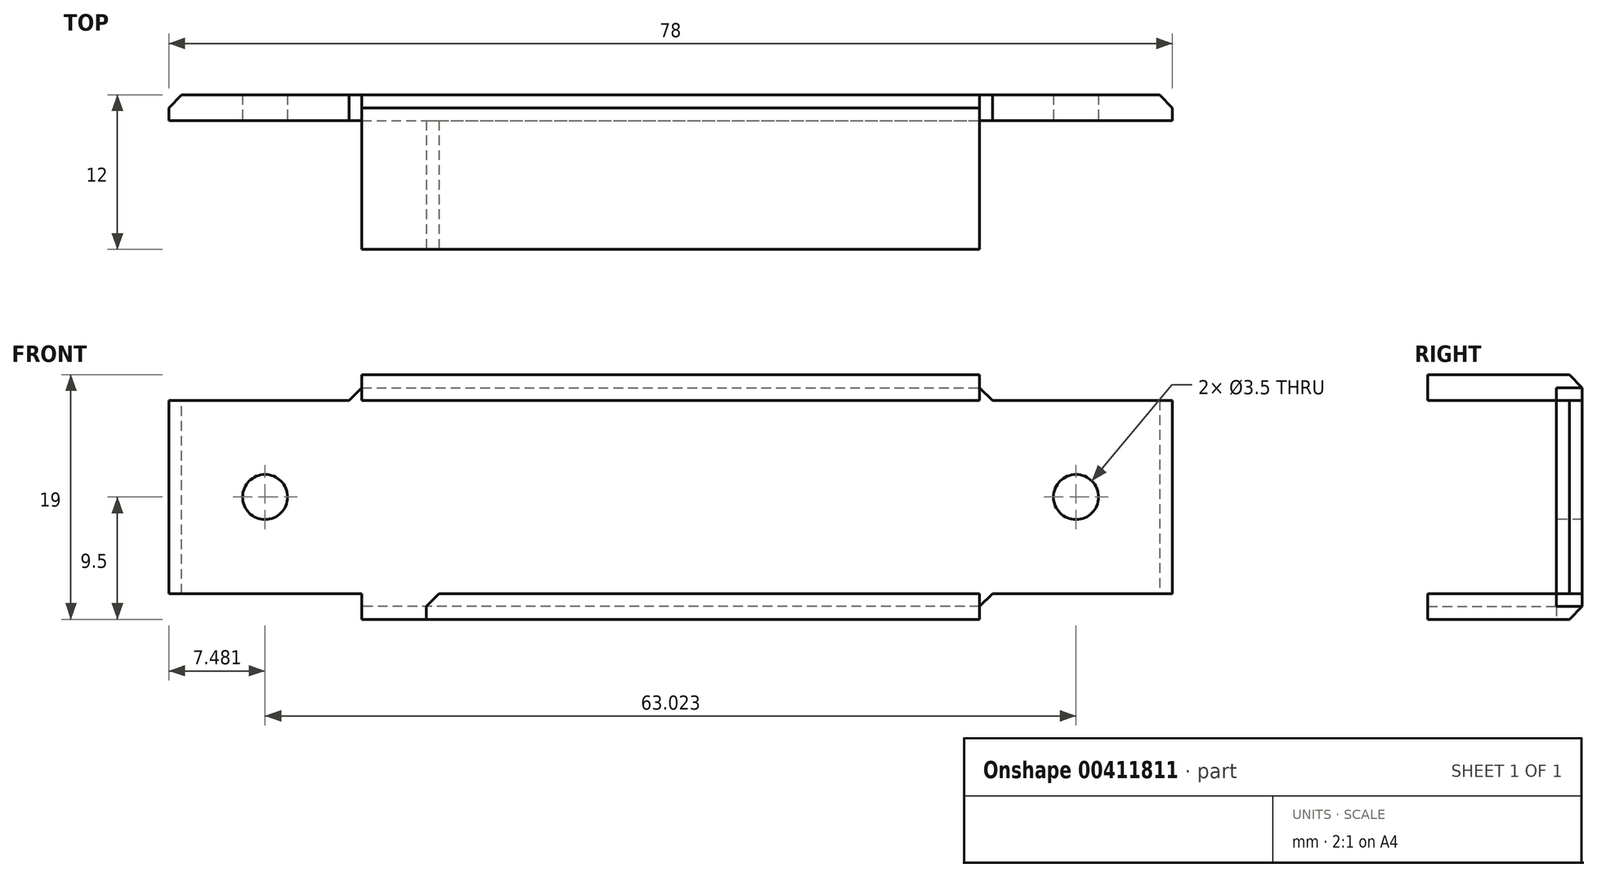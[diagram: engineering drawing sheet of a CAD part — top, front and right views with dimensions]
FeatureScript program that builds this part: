
annotation { "Feature Type Name" : "Feature", "Feature Type Description" : "" }
export const myFeature = defineFeature(function(context is Context, id is Id, definition is map)
    precondition{}
    {
        {
            var Q0;
            Q0=qCreatedBy(makeId("Top.planeOp"),FACE);
            var sketch = newSketch(context, id + "F0", { "sketchPlane" : qUnion([Q0])});
            skLineSegment(sketch, "E0.bottom", {"start": v(-35.57, 12) * mm, "end": v(42.43, 12) * mm});
            skLineSegment(sketch, "E0.top", {"start": v(-35.57, 0) * mm, "end": v(42.43, 0) * mm});
            skLineSegment(sketch, "E0.left", {"start": v(-35.57, 12) * mm, "end": v(-35.57, 0) * mm});
            skLineSegment(sketch, "E0.right", {"start": v(42.43, 12) * mm, "end": v(42.43, 0) * mm});
            skSolve(sketch);
        }
        {
            var Q0;
            Q0 = qSketchRegion(id + "F0", true);
            extrude(context, id + "F1", {"entities" : qUnion([Q0]), "oppositeDirection" : true, "depth" : 19 * mm});
        }
        {
            var Q0;
            Q0=makeQuery(id+"F1.opExtrude","SWEPT_FACE",FACE,{"disambiguationData":[OSD([sQuery(id+"F0.wireOp",EDGE,"E0.top")])]});
            var sketch = newSketch(context, id + "F2", { "sketchPlane" : qUnion([Q0])});
            skLineSegment(sketch, "E1", {"start": v(-20.57, -17) * mm, "end": v(-20.57, -19) * mm});
            skLineSegment(sketch, "E2", {"start": v(27.43, 0) * mm, "end": v(27.43, -2) * mm});
            skLineSegment(sketch, "E3", {"start": v(-35.61, -2) * mm, "end": v(27.43, -2) * mm});
            skLineSegment(sketch, "E4", {"start": v(-15.57, -17) * mm, "end": v(27.43, -17) * mm});
            skPoint(sketch, "E5.orphan", {"position": v(-20.57, 0) * mm});
            skLineSegment(sketch, "E6.trimOffspring", {"start": v(27.43, -17) * mm, "end": v(27.43, -19) * mm});
            skLineSegment(sketch, "E7", {"start": v(-20.57, -17) * mm, "end": v(-35.57, -17) * mm});
            skLineSegment(sketch, "E8", {"start": v(27.43, -2) * mm, "end": v(42.43, -2) * mm});
            skLineSegment(sketch, "E9", {"start": v(27.43, -17) * mm, "end": v(42.43, -17) * mm});
            skLineSegment(sketch, "E10", {"start": v(-15.57, -17) * mm, "end": v(-15.57, -19) * mm});
            skLineSegment(sketch, "E11", {"start": v(-20.57, 0) * mm, "end": v(-20.57, -2) * mm});
            skLineSegment(sketch, "E12", {"start": v(-35.61, -2) * mm, "end": v(-35.57, 0) * mm});
            skLineSegment(sketch, "E13", {"start": v(-35.57, 0) * mm, "end": v(-20.57, 0) * mm});
            skLineSegment(sketch, "E14.bottom", {"start": v(-35.61, -2) * mm, "end": v(-20.57, -2) * mm});
            skLineSegment(sketch, "E14.right", {"start": v(-20.57, -2) * mm, "end": v(-20.57, 0) * mm});
            skCircle(sketch, "E15", {"center": v(34.93, -9.5) * mm, "radius": 1.75 * mm});
            skPoint(sketch, "E15.centerSnap0", {"position": v(34.93, -2) * mm});
            skCircle(sketch, "E16", {"center": v(-28.09, -9.5) * mm, "radius": 1.75 * mm});
            skPoint(sketch, "E16.centerSnap0", {"position": v(-28.09, -2) * mm});
            skSolve(sketch);
        }
        {
            var Q0;
            {var subQ10=sQuery(id+"F2.wireOp",EDGE,"E1");Q0=makeQuery(id+"F2.imprint","IMPRINT",FACE,{"disambiguationData":[TD([[makeQuery(id+"F2.imprint","IMPRINT",EDGE,{"derivedFrom":subQ10}),1.0]])]});}
            extrude(context, id + "F3", {"entities" : qUnion([Q0]), "operationType" : NewBodyOperationType.REMOVE, "oppositeDirection" : true, "depth" : 10 * mm});
        }
        {
            var Q0;
            {var subQ1=sQuery(id+"F0.wireOp",EDGE,"E0.top");Q0=makeQuery(id+"F3.boolean.opBoolean","SPLIT",FACE,{"disambiguationData":[TD([makeQuery(id+"F3.opExtrude","SWEPT_FACE",FACE,{"disambiguationData":[OSD([sQuery(id+"F2.wireOp",EDGE,"E1")])]})])],"derivedFrom":makeQuery(id+"F1.opExtrude","SWEPT_FACE",FACE,{"disambiguationData":[OSD([subQ1])]})});}
            var Q1;
            {var subQ0=sQuery(id+"F2.wireOp",EDGE,"E13");Q1=makeQuery(id+"F2.imprint","IMPRINT",FACE,{"disambiguationData":[TD([[makeQuery(id+"F2.imprint","IMPRINT",EDGE,{"derivedFrom":subQ0}),-1.0]])]});}
            var Q2;
            {var subQ0=sQuery(id+"F2.wireOp",EDGE,"E2");Q2=makeQuery(id+"F2.imprint","IMPRINT",FACE,{"disambiguationData":[TD([[makeQuery(id+"F2.imprint","IMPRINT",EDGE,{"derivedFrom":subQ0}),1.0]])]});}
            var Q3;
            {var subQ0=sQuery(id+"F2.wireOp",EDGE,"E6.trimOffspring");Q3=makeQuery(id+"F2.imprint","IMPRINT",FACE,{"disambiguationData":[TD([[makeQuery(id+"F2.imprint","IMPRINT",EDGE,{"derivedFrom":subQ0}),1.0]])]});}
            var Q4;
            Q4=makeQuery(id+"F2.imprint","IMPRINT",FACE,{"disambiguationData":[TD([[makeQuery(id+"F2.imprint","IMPRINT",EDGE,{"derivedFrom":sQuery(id+"F2.wireOp",EDGE,"E16")}),1.0]])]});
            var Q5;
            Q5=makeQuery(id+"F2.imprint","IMPRINT",FACE,{"disambiguationData":[TD([[makeQuery(id+"F2.imprint","IMPRINT",EDGE,{"derivedFrom":sQuery(id+"F2.wireOp",EDGE,"E15")}),1.0]])]});
            extrude(context, id + "F4", {"entities" : qUnion([Q0, Q1, Q2, Q3, Q4, Q5]), "operationType" : NewBodyOperationType.REMOVE, "endBound" : BoundingType.UP_TO_NEXT, "oppositeDirection" : true, "depth" : 25 * mm});
        }
        {
            var Q0;
            Q0=makeQuery(id+"F4.boolean.opBoolean","COPY",EDGE,{"derivedFrom":makeQuery(id+"F4.opExtrude","TWEAK_EDGE",EDGE,{"derivedFrom":[makeQuery(id+"F1.opExtrude","SWEPT_FACE",FACE,{"disambiguationData":[OSD([sQuery(id+"F0.wireOp",EDGE,"E0.bottom")])]}),makeQuery(id+"F3.boolean.opBoolean","COPY",EDGE,{"derivedFrom":makeQuery(id+"F3.opExtrude","CAP_EDGE",EDGE,{"disambiguationData":[OSD([sQuery(id+"F2.wireOp",EDGE,"E7")])],"isStart":true})})]})});
            var Q1;
            Q1=makeQuery(id+"F1.opExtrude","SWEPT_EDGE",EDGE,{"disambiguationData":[OSD([sQuery(id+"F0.wireOp",EDGE,"E0.bottom"),sQuery(id+"F0.wireOp",EDGE,"E0.left")])]});
            var Q2;
            {var subQ0=sQuery(id+"F2.wireOp",EDGE,"E14.bottom");Q2=makeQuery(id+"F4.boolean.opBoolean","COPY",EDGE,{"derivedFrom":makeQuery(id+"F4.opExtrude","TWEAK_EDGE",EDGE,{"derivedFrom":[makeQuery(id+"F1.opExtrude","SWEPT_FACE",FACE,{"disambiguationData":[OSD([sQuery(id+"F0.wireOp",EDGE,"E0.bottom")])]}),makeQuery(id+"F2.imprint","IMPRINT",EDGE,{"disambiguationData":[TD([[makeQuery(id+"F2.imprint","INTERSECT",VERTEX,{"derivedFrom":[sQuery(id+"F2.wireOp",EDGE,"E3"),subQ0,sQuery(id+"F2.wireOp",EDGE,"E14.right")]}),1.0]])],"derivedFrom":subQ0})]})});}
            var Q3;
            Q3=makeQuery(id+"F1.opExtrude","CAP_EDGE",EDGE,{"disambiguationData":[OSD([sQuery(id+"F0.wireOp",EDGE,"E0.bottom")])],"isStart":false});
            var Q4;
            Q4=makeQuery(id+"F4.boolean.opBoolean","COPY",EDGE,{"derivedFrom":makeQuery(id+"F4.opExtrude","TWEAK_EDGE",EDGE,{"derivedFrom":[makeQuery(id+"F1.opExtrude","SWEPT_FACE",FACE,{"disambiguationData":[OSD([sQuery(id+"F0.wireOp",EDGE,"E0.bottom")])]}),makeQuery(id+"F2.imprint","IMPRINT",EDGE,{"derivedFrom":sQuery(id+"F2.wireOp",EDGE,"E9")})]})});
            var Q5;
            Q5=makeQuery(id+"F1.opExtrude","SWEPT_EDGE",EDGE,{"disambiguationData":[OSD([sQuery(id+"F0.wireOp",EDGE,"E0.bottom"),sQuery(id+"F0.wireOp",EDGE,"E0.right")])]});
            var Q6;
            Q6=makeQuery(id+"F4.boolean.opBoolean","COPY",EDGE,{"derivedFrom":makeQuery(id+"F4.opExtrude","TWEAK_EDGE",EDGE,{"derivedFrom":[makeQuery(id+"F1.opExtrude","SWEPT_FACE",FACE,{"disambiguationData":[OSD([sQuery(id+"F0.wireOp",EDGE,"E0.bottom")])]}),makeQuery(id+"F2.imprint","IMPRINT",EDGE,{"derivedFrom":sQuery(id+"F2.wireOp",EDGE,"E8")})]})});
            var Q7;
            Q7=makeQuery(id+"F1.opExtrude","CAP_EDGE",EDGE,{"disambiguationData":[OSD([sQuery(id+"F0.wireOp",EDGE,"E0.bottom")])],"isStart":true});
            var Q8;
            Q8=makeQuery(id+"F3.boolean.opBoolean","COPY",EDGE,{"derivedFrom":makeQuery(id+"F3.opExtrude","CAP_EDGE",EDGE,{"disambiguationData":[OSD([sQuery(id+"F2.wireOp",EDGE,"E3"),sQuery(id+"F2.wireOp",EDGE,"E8"),sQuery(id+"F2.wireOp",EDGE,"E14.bottom")])],"isStart":true})});
            var Q9;
            Q9=makeQuery(id+"F3.boolean.opBoolean","COPY",EDGE,{"derivedFrom":makeQuery(id+"F3.opExtrude","CAP_EDGE",EDGE,{"disambiguationData":[OSD([sQuery(id+"F2.wireOp",EDGE,"E4"),sQuery(id+"F2.wireOp",EDGE,"E9")])],"isStart":true})});
            var Q10;
            {var subQ0=sQuery(id+"F2.wireOp",EDGE,"E9");var subQ1=sQuery(id+"F2.wireOp",EDGE,"E4");var subQ2=sQuery(id+"F2.wireOp",EDGE,"E6.trimOffspring");Q10=makeQuery(id+"F4.boolean.opBoolean","COPY",EDGE,{"disambiguationData":[topologyDisambiguationEdgeConnected([makeQuery(id+"F3.boolean.opBoolean","COPY",FACE,{"derivedFrom":makeQuery(id+"F3.opExtrude","SWEPT_FACE",FACE,{"disambiguationData":[OSD([subQ1,subQ0])]})})])],"derivedFrom":makeQuery(id+"F4.opExtrude","SWEPT_EDGE",EDGE,{"disambiguationData":[OSD([subQ1,subQ2,subQ0])]})});}
            var Q11;
            {var subQ0=sQuery(id+"F2.wireOp",EDGE,"E8");var subQ1=sQuery(id+"F2.wireOp",EDGE,"E3");var subQ2=sQuery(id+"F2.wireOp",EDGE,"E2");Q11=makeQuery(id+"F4.boolean.opBoolean","COPY",EDGE,{"disambiguationData":[topologyDisambiguationEdgeConnected([makeQuery(id+"F3.boolean.opBoolean","COPY",FACE,{"derivedFrom":makeQuery(id+"F3.opExtrude","SWEPT_FACE",FACE,{"disambiguationData":[OSD([subQ1,subQ0,sQuery(id+"F2.wireOp",EDGE,"E14.bottom")])]})})])],"derivedFrom":makeQuery(id+"F4.opExtrude","SWEPT_EDGE",EDGE,{"disambiguationData":[OSD([subQ2,subQ1,subQ0])]})});}
            var Q12;
            Q12=makeQuery(id+"F3.boolean.opBoolean","COPY",EDGE,{"derivedFrom":makeQuery(id+"F3.opExtrude","SWEPT_EDGE",EDGE,{"disambiguationData":[OSD([sQuery(id+"F2.wireOp",EDGE,"E4"),sQuery(id+"F2.wireOp",EDGE,"E10")])]})});
            var Q13;
            {var subQ0=sQuery(id+"F2.wireOp",EDGE,"E14.bottom");var subQ1=sQuery(id+"F2.wireOp",EDGE,"E3");var subQ2=sQuery(id+"F2.wireOp",EDGE,"E14.right");Q13=makeQuery(id+"F4.boolean.opBoolean","COPY",EDGE,{"disambiguationData":[topologyDisambiguationEdgeConnected([makeQuery(id+"F3.boolean.opBoolean","COPY",FACE,{"derivedFrom":makeQuery(id+"F3.opExtrude","SWEPT_FACE",FACE,{"disambiguationData":[OSD([subQ1,sQuery(id+"F2.wireOp",EDGE,"E8"),subQ0])]})})])],"derivedFrom":makeQuery(id+"F4.opExtrude","SWEPT_EDGE",EDGE,{"disambiguationData":[OSD([subQ1,subQ0,subQ2])]})});}
            chamfer(context, id + "F5", {"entities" : qUnion([Q0, Q1, Q2, Q3, Q4, Q5, Q6, Q7, Q8, Q9, Q10, Q11, Q12, Q13]), "width" : 1 * mm, "tangentPropagation" : true});
        }
    });
